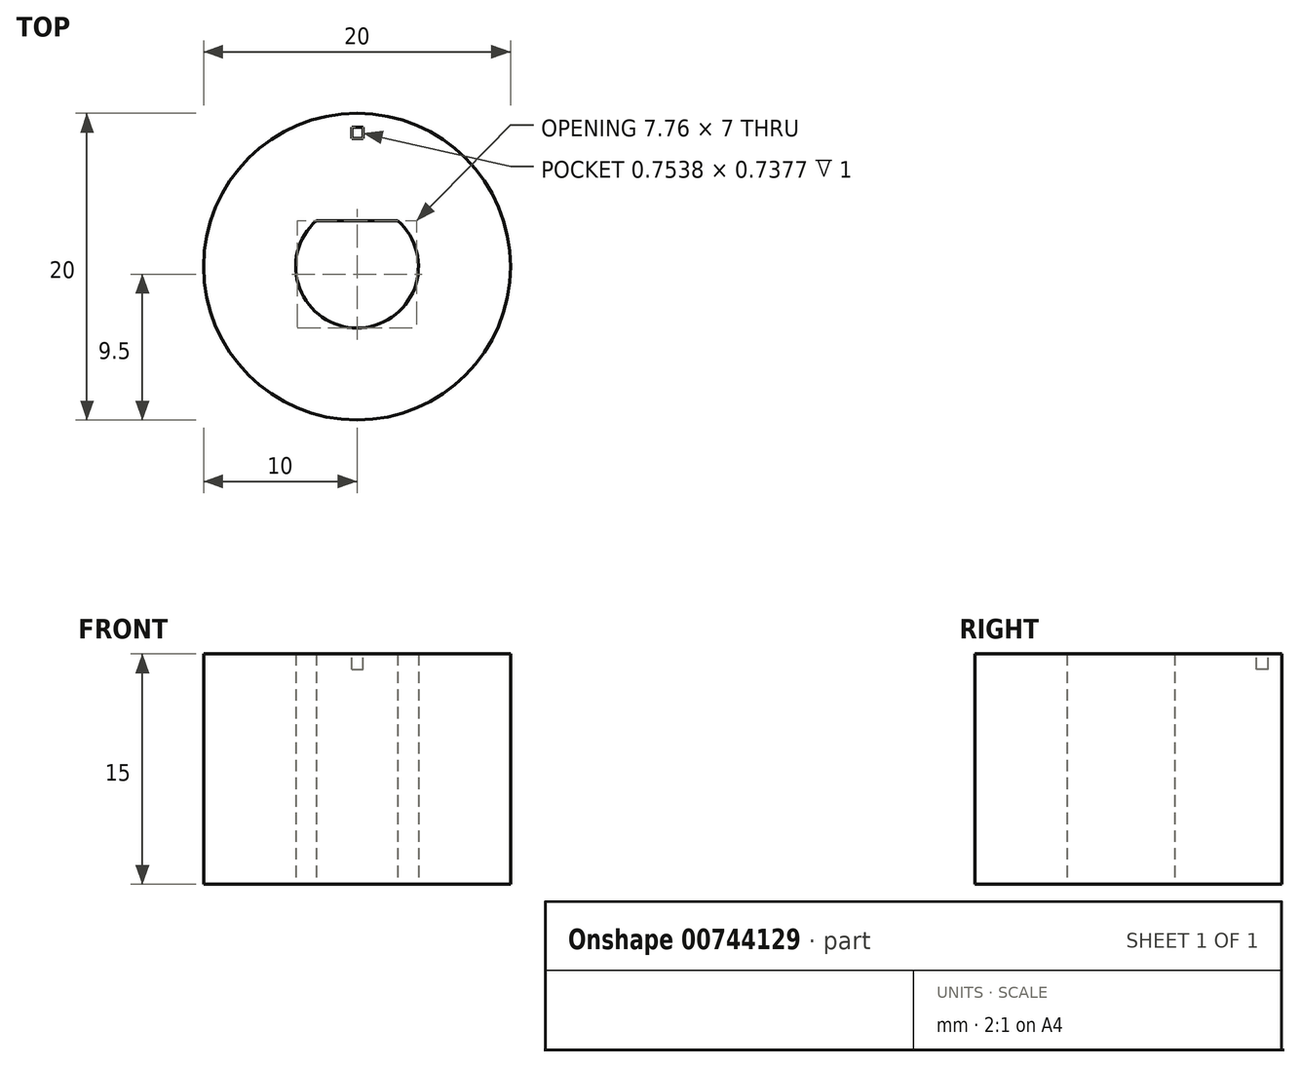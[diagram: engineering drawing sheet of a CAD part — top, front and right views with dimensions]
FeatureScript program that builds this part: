
annotation { "Feature Type Name" : "Feature", "Feature Type Description" : "" }
export const myFeature = defineFeature(function(context is Context, id is Id, definition is map)
    precondition{}
    {
        {
            var Q0;
            Q0=qCreatedBy(makeId("Top.planeOp"),FACE);
            var sketch = newSketch(context, id + "F0", { "sketchPlane" : qUnion([Q0])});
            skCircle(sketch, "E0", {"center": v(0, 0) * mm, "radius": 10 * mm});
            skArc(sketch, "E1", {"start": v(-2.65, 3) * mm, "mid": v(0, -4) * mm, "end": v(2.65, 3) * mm});
            skLineSegment(sketch, "E2", {"start": v(-2.65, 3) * mm, "end": v(2.65, 3) * mm});
            skSolve(sketch);
        }
        {
            var Q0;
            Q0=makeQuery(id+"F0.imprint","IMPRINT",FACE,{"disambiguationData":[TD([[makeQuery(id+"F0.imprint","IMPRINT",EDGE,{"derivedFrom":sQuery(id+"F0.wireOp",EDGE,"E0")}),1.0]])]});
            extrude(context, id + "F1", {"entities" : qUnion([Q0]), "depth" : 15 * mm, "offsetDistance" : 25 * mm});
        }
        {
            var Q0;
            Q0=makeQuery(id+"F1.opExtrude","CAP_FACE",FACE,{"disambiguationData":[OSD([sQuery(id+"F0.wireOp",EDGE,"E0"),sQuery(id+"F0.wireOp",EDGE,"E1"),sQuery(id+"F0.wireOp",EDGE,"E2")])],"isStart":false});
            var sketch = newSketch(context, id + "F2", { "sketchPlane" : qUnion([Q0])});
            skLineSegment(sketch, "E3.bottom", {"start": v(-0.35, 9.09) * mm, "end": v(0.4, 9.09) * mm});
            skLineSegment(sketch, "E3.top", {"start": v(-0.35, 8.35) * mm, "end": v(0.4, 8.35) * mm});
            skLineSegment(sketch, "E3.left", {"start": v(-0.35, 9.09) * mm, "end": v(-0.35, 8.35) * mm});
            skLineSegment(sketch, "E3.right", {"start": v(0.4, 9.09) * mm, "end": v(0.4, 8.35) * mm});
            skSolve(sketch);
        }
        {
            var Q0;
            Q0=makeQuery(id+"F2.imprint","IMPRINT",FACE,{"disambiguationData":[TD([[makeQuery(id+"F2.imprint","IMPRINT",EDGE,{"derivedFrom":sQuery(id+"F2.wireOp",EDGE,"E3.bottom")}),-1.0]])]});
            extrude(context, id + "F3", {"entities" : qUnion([Q0]), "operationType" : NewBodyOperationType.REMOVE, "oppositeDirection" : true, "depth" : 1 * mm, "offsetDistance" : 25 * mm});
        }
    });
